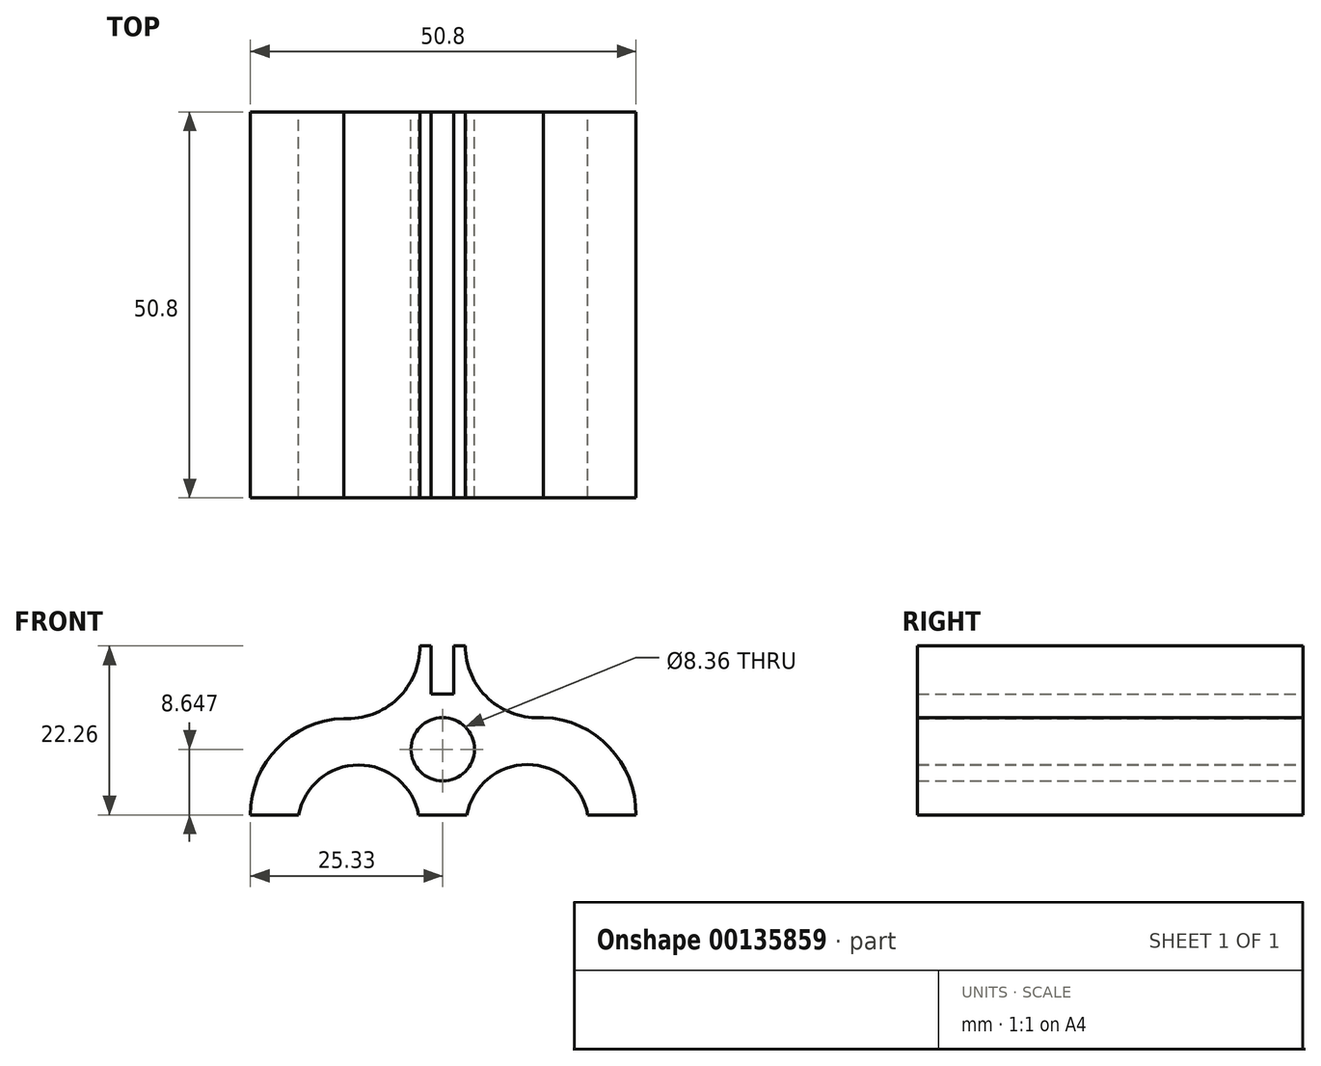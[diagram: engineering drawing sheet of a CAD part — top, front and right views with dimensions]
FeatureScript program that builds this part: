
annotation { "Feature Type Name" : "Feature", "Feature Type Description" : "" }
export const myFeature = defineFeature(function(context is Context, id is Id, definition is map)
    precondition{}
    {
        {
            var Q0;
            Q0=qCreatedBy(makeId("Front.planeOp"),FACE);
            var sketch = newSketch(context, id + "F0", { "sketchPlane" : qUnion([Q0])});
            skArc(sketch, "E0", {"start": v(25.47, 0) * mm, "mid": v(21.78, 9.1) * mm, "end": v(12.7, 12.84) * mm});
            skLineSegment(sketch, "E1", {"start": v(-12.77, 12.7) * mm, "end": v(-11.82, 12.7) * mm});
            skLineSegment(sketch, "E2", {"start": v(-25.33, 0) * mm, "end": v(-18.98, 0) * mm});
            skArc(sketch, "E3.trimOffspring", {"start": v(-12.63, 12.7) * mm, "mid": v(-21.6, 8.98) * mm, "end": v(-25.33, 0) * mm});
            skArc(sketch, "E4", {"start": v(2.96, 22.28) * mm, "mid": v(6.03, 15.31) * mm, "end": v(13.24, 12.83) * mm});
            skArc(sketch, "E5", {"start": v(-13.05, 12.7) * mm, "mid": v(-5.96, 15.3) * mm, "end": v(-3, 22.25) * mm});
            skLineSegment(sketch, "E6.top", {"start": v(-1.52, 15.9) * mm, "end": v(1.48, 15.9) * mm});
            skLineSegment(sketch, "E6.left", {"start": v(-1.52, 22.25) * mm, "end": v(-1.52, 15.9) * mm});
            skLineSegment(sketch, "E6.right", {"start": v(1.48, 22.25) * mm, "end": v(1.48, 15.9) * mm});
            skLineSegment(sketch, "E7", {"start": v(-3, 22.25) * mm, "end": v(-1.52, 22.25) * mm});
            skLineSegment(sketch, "E8", {"start": v(1.48, 22.25) * mm, "end": v(2.96, 22.26) * mm});
            skLineSegment(sketch, "E9.trimOffspring", {"start": v(11.69, 12.83) * mm, "end": v(12.7, 12.84) * mm});
            skLineSegment(sketch, "E10.trimOffspring", {"start": v(19.12, 0) * mm, "end": v(25.47, 0) * mm});
            skLineSegment(sketch, "E11", {"start": v(0, 0) * mm, "end": v(-3.18, 0) * mm});
            skLineSegment(sketch, "E12", {"start": v(0, 0) * mm, "end": v(3.18, 0) * mm});
            skArc(sketch, "E13", {"start": v(-3.18, 0) * mm, "mid": v(-11.08, 6.59) * mm, "end": v(-18.98, 0) * mm});
            skArc(sketch, "E14", {"start": v(19.12, 0) * mm, "mid": v(11.15, 6.63) * mm, "end": v(3.18, 0) * mm});
            skCircle(sketch, "E15", {"center": v(0, 8.65) * mm, "radius": 4.18 * mm});
            skSolve(sketch);
        }
        {
            var Q0;
            {var subQ10=sQuery(id+"F0.wireOp",EDGE,"E2");Q0=makeQuery(id+"F0.imprint","IMPRINT",FACE,{"disambiguationData":[TD([[makeQuery(id+"F0.imprint","IMPRINT",EDGE,{"derivedFrom":subQ10}),1.0]])]});}
            extrude(context, id + "F1", {"entities" : qUnion([Q0]), "depth" : 50.8 * mm});
        }
    });
